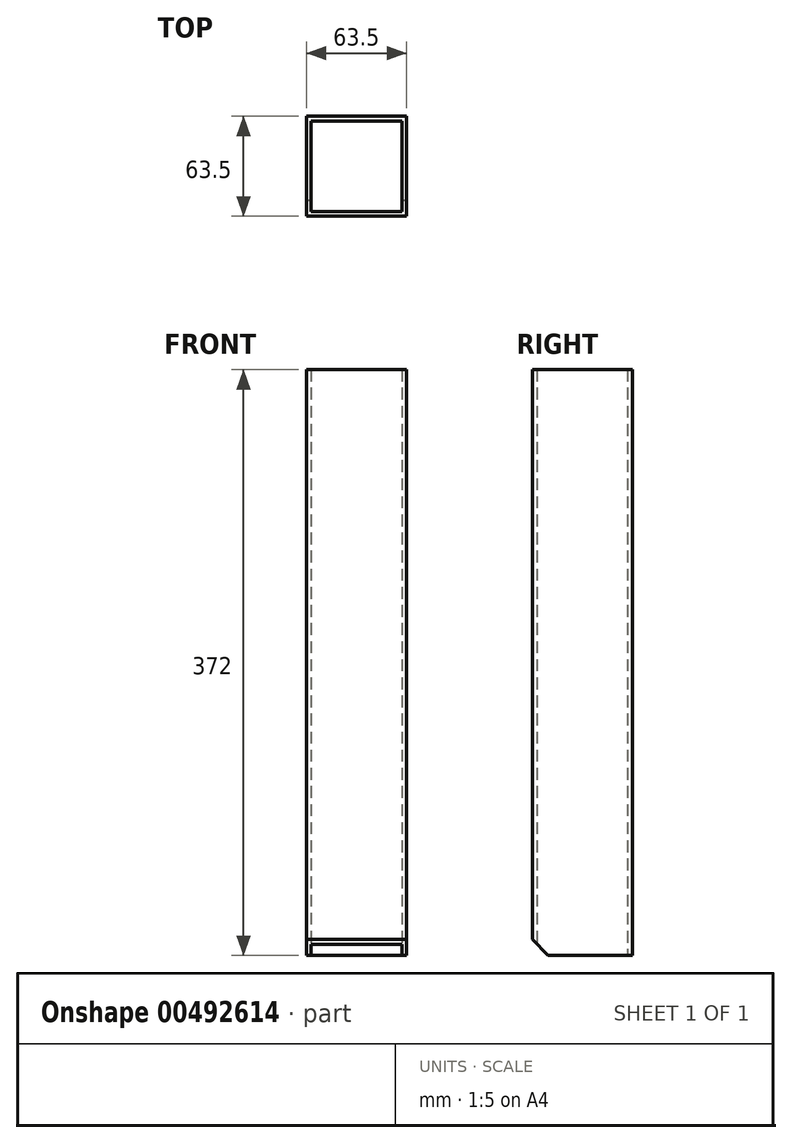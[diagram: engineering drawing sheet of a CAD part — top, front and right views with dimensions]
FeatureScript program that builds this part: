
annotation { "Feature Type Name" : "Feature", "Feature Type Description" : "" }
export const myFeature = defineFeature(function(context is Context, id is Id, definition is map)
    precondition{}
    {
        {
            var Q0;
            Q0=qCreatedBy(makeId("Top.planeOp"),FACE);
            var sketch = newSketch(context, id + "F0", { "sketchPlane" : qUnion([Q0])});
            skLineSegment(sketch, "E0.bottom", {"start": v(-27.08, 37.92) * mm, "end": v(36.42, 37.92) * mm});
            skLineSegment(sketch, "E0.top", {"start": v(-27.08, -25.58) * mm, "end": v(36.42, -25.58) * mm});
            skLineSegment(sketch, "E0.left", {"start": v(-27.08, 37.92) * mm, "end": v(-27.08, -25.58) * mm});
            skLineSegment(sketch, "E0.right", {"start": v(36.42, 37.92) * mm, "end": v(36.42, -25.58) * mm});
            skLineSegment(sketch, "E1.bottom", {"start": v(-24.08, 34.92) * mm, "end": v(33.42, 34.92) * mm});
            skLineSegment(sketch, "E1.top", {"start": v(-24.08, -22.58) * mm, "end": v(33.42, -22.58) * mm});
            skLineSegment(sketch, "E1.left", {"start": v(-24.08, 34.92) * mm, "end": v(-24.08, -22.58) * mm});
            skLineSegment(sketch, "E1.right", {"start": v(33.42, 34.92) * mm, "end": v(33.42, -22.58) * mm});
            skSolve(sketch);
        }
        {
            var Q0;
            Q0 = qSketchRegion(id + "F0", true);
            extrude(context, id + "F1", {"entities" : qUnion([Q0]), "offsetDistance" : 25 * mm, "depth" : 372 * mm});
        }
        {
            var Q0;
            Q0=makeQuery(id+"F1.opExtrude","CAP_EDGE",EDGE,{"disambiguationData":[OSD([sQuery(id+"F0.wireOp",EDGE,"E0.top")])],"isStart":true});
            chamfer(context, id + "F2", {"entities" : qUnion([Q0]), "width" : 10 * mm, "tangentPropagation" : true});
        }
    });
